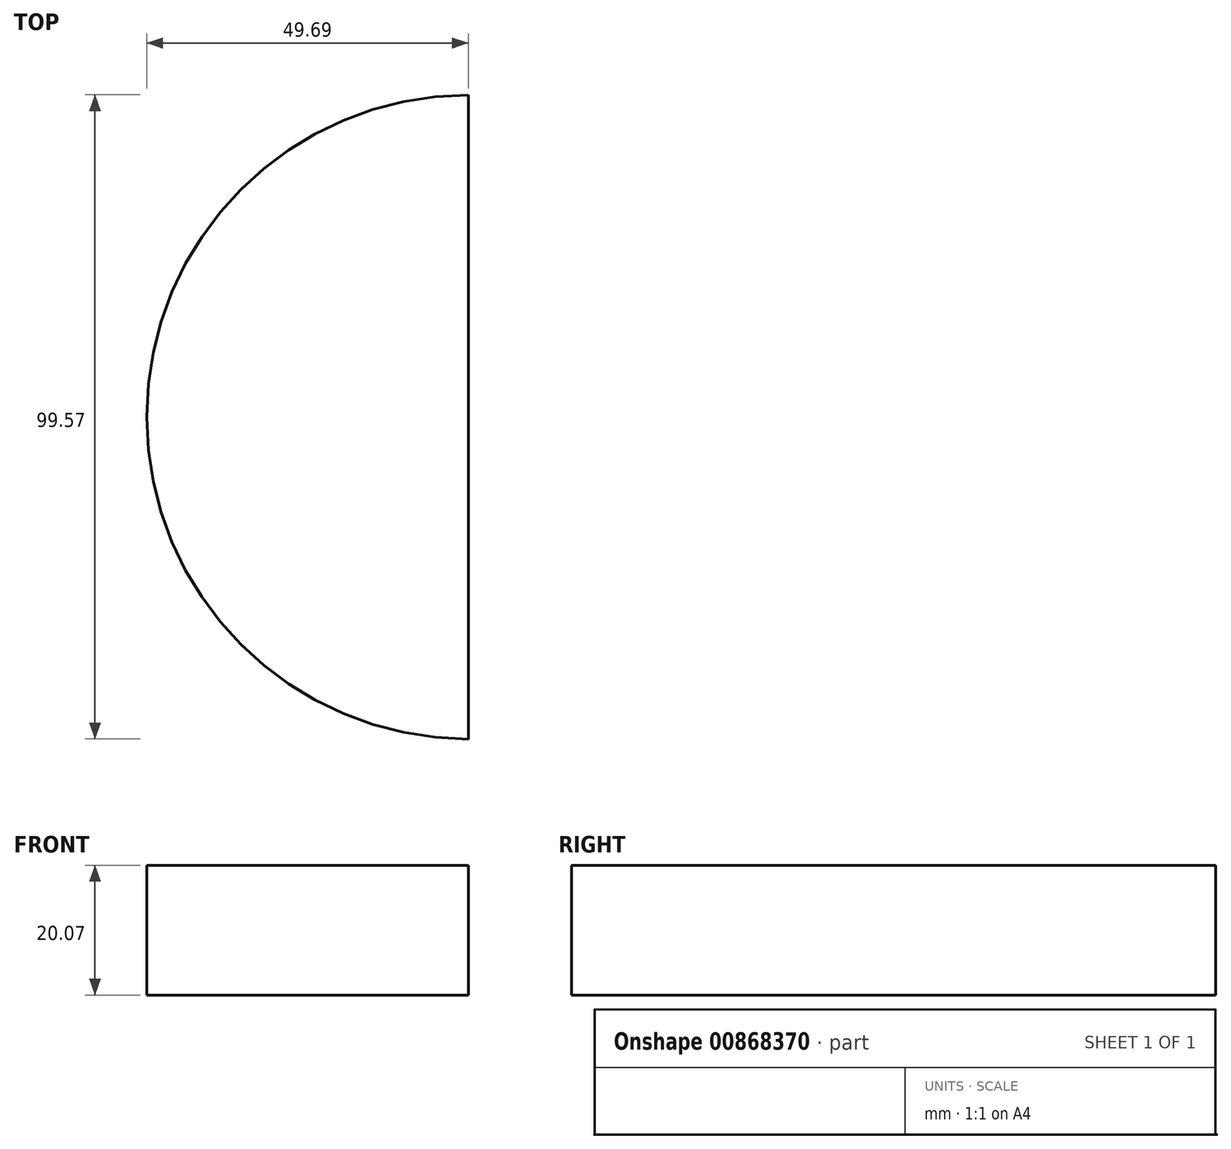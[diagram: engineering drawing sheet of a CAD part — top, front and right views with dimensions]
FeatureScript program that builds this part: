
annotation { "Feature Type Name" : "Feature", "Feature Type Description" : "" }
export const myFeature = defineFeature(function(context is Context, id is Id, definition is map)
    precondition{}
    {
        {
            var Q0;
            Q0=qCreatedBy(makeId("Top.planeOp"),FACE);
            var sketch = newSketch(context, id + "F0", { "sketchPlane" : qUnion([Q0])});
            skCircle(sketch, "E0", {"center": v(0, 0) * mm, "radius": 49.91 * mm});
            skSolve(sketch);
        }
        {
            var Q0;
            Q0=makeQuery(id+"F0.imprint","IMPRINT",FACE,{"disambiguationData":[TD([[makeQuery(id+"F0.imprint","IMPRINT",EDGE,{"derivedFrom":sQuery(id+"F0.wireOp",EDGE,"E0")}),1.0]])]});
            extrude(context, id + "F1", {"entities" : qUnion([Q0]), "depth" : 99.82 * mm, "offsetDistance" : 25.4 * mm});
        }
        {
            var Q0;
            Q0=qCreatedBy(makeId("Top.planeOp"),FACE);
            var sketch = newSketch(context, id + "F2", { "sketchPlane" : qUnion([Q0])});
            skArc(sketch, "E1", {"start": v(0, 49.96) * mm, "mid": v(-49.69, 0.17) * mm, "end": v(0, -49.61) * mm});
            skLineSegment(sketch, "E2", {"start": v(0, -49.61) * mm, "end": v(0, 49.96) * mm});
            skSolve(sketch);
        }
        {
            var Q0;
            Q0=makeQuery(id+"F1.opExtrude","SWEPT_BODY",BODY,{"disambiguationData":[OSD([sQuery(id+"F0.wireOp",EDGE,"E0")])]});
            deleteBodies(context, id + "F3", {"entities" : qUnion([Q0])});
        }
        {
            var Q0;
            Q0=makeQuery(id+"F2.imprint","IMPRINT",FACE,{"disambiguationData":[TD([[makeQuery(id+"F2.imprint","IMPRINT",EDGE,{"derivedFrom":sQuery(id+"F2.wireOp",EDGE,"E1")}),1.0]])]});
            extrude(context, id + "F4", {"entities" : qUnion([Q0]), "depth" : 20.07 * mm, "offsetDistance" : 25.4 * mm});
        }
    });
